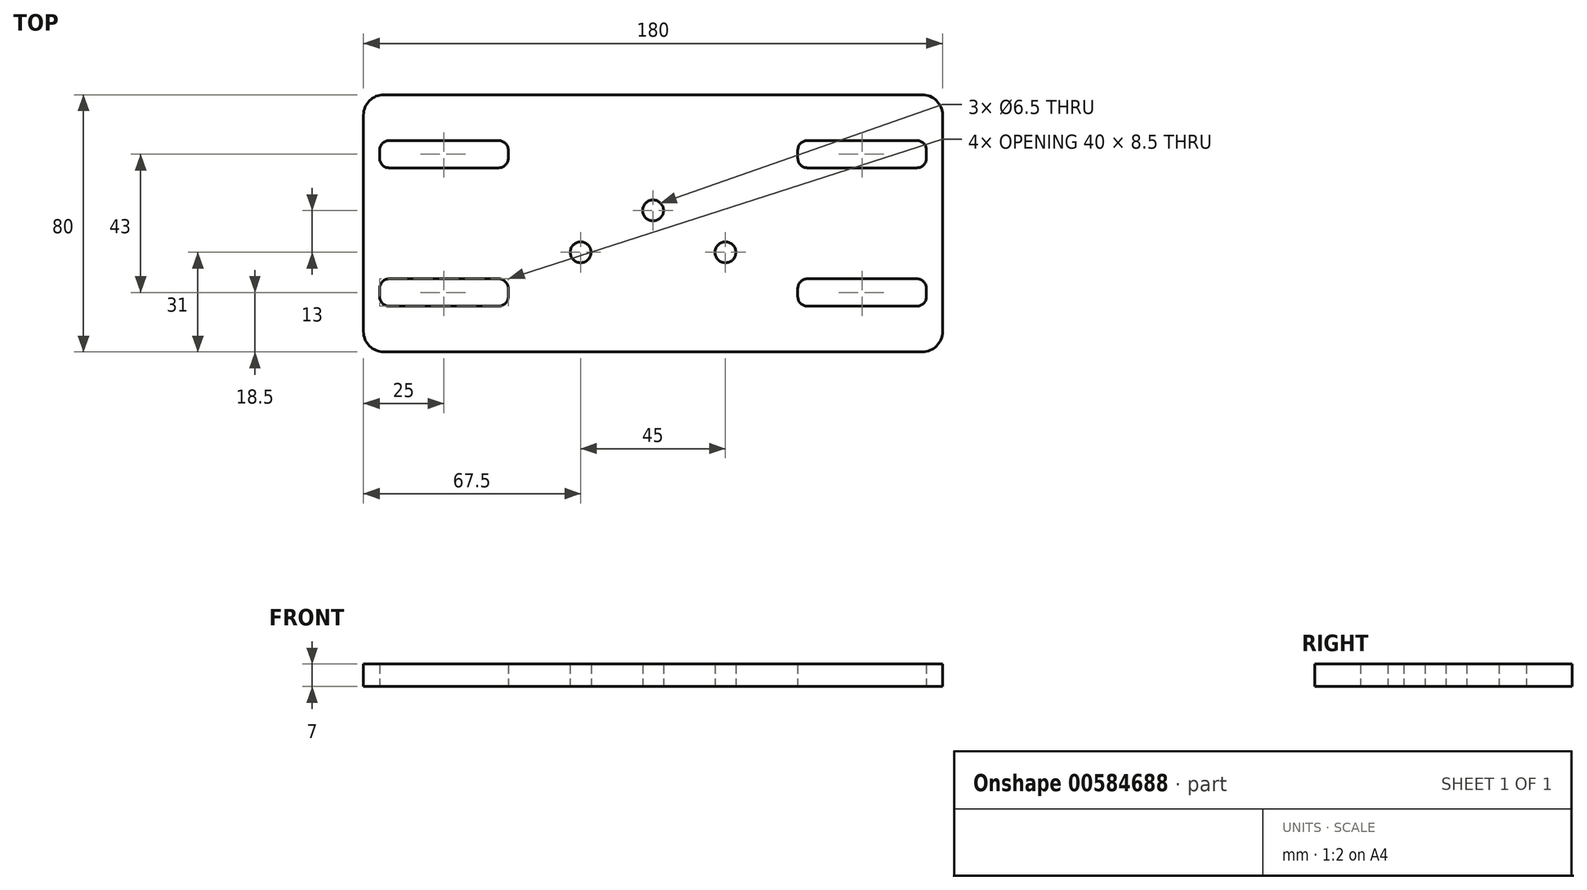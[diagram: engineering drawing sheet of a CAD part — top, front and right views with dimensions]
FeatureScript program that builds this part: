
annotation { "Feature Type Name" : "Feature", "Feature Type Description" : "" }
export const myFeature = defineFeature(function(context is Context, id is Id, definition is map)
    precondition{}
    {
        {
            var Q0;
            Q0=qCreatedBy(makeId("Top.planeOp"),FACE);
            var sketch = newSketch(context, id + "F0", { "sketchPlane" : qUnion([Q0])});
            skLineSegment(sketch, "E0.bottom", {"start": v(-83.65, 17.92) * mm, "end": v(83.65, 17.92) * mm});
            skLineSegment(sketch, "E0.top", {"start": v(-83.65, -62.08) * mm, "end": v(83.65, -62.08) * mm});
            skLineSegment(sketch, "E0.left", {"start": v(-90, 11.57) * mm, "end": v(-90, -55.73) * mm});
            skLineSegment(sketch, "E0.right", {"start": v(90, 11.57) * mm, "end": v(90, -55.73) * mm});
            skLineSegment(sketch, "E1.bottom", {"start": v(-82, -39.33) * mm, "end": v(-48, -39.33) * mm});
            skLineSegment(sketch, "E1.top", {"start": v(-82, -47.83) * mm, "end": v(-48, -47.83) * mm});
            skLineSegment(sketch, "E1.left", {"start": v(-85, -42.33) * mm, "end": v(-85, -44.83) * mm});
            skLineSegment(sketch, "E1.right", {"start": v(-45, -42.33) * mm, "end": v(-45, -44.83) * mm});
            skLineSegment(sketch, "E2", {"start": v(-120.35, -22.08) * mm, "end": v(115.73, -22.08) * mm, "construction": true});
            skPoint(sketch, "E3.visualSharp", {"position": v(-45, -39.33) * mm});
            skArc(sketch, "E3.filletArc", {"start": v(-45, -42.33) * mm, "mid": v(-45.88, -40.2) * mm, "end": v(-48, -39.33) * mm});
            skPoint(sketch, "E4.visualSharp", {"position": v(-45, -47.83) * mm});
            skArc(sketch, "E4.filletArc", {"start": v(-48, -47.83) * mm, "mid": v(-45.88, -46.95) * mm, "end": v(-45, -44.83) * mm});
            skPoint(sketch, "E5.visualSharp", {"position": v(-85, -47.83) * mm});
            skArc(sketch, "E5.filletArc", {"start": v(-85, -44.83) * mm, "mid": v(-84.12, -46.95) * mm, "end": v(-82, -47.83) * mm});
            skPoint(sketch, "E6.visualSharp", {"position": v(-85, -39.33) * mm});
            skArc(sketch, "E6.filletArc", {"start": v(-82, -39.33) * mm, "mid": v(-84.12, -40.2) * mm, "end": v(-85, -42.33) * mm});
            skCircle(sketch, "E7", {"center": v(0, -18.08) * mm, "radius": 3.25 * mm});
            skCircle(sketch, "E8", {"center": v(-22.5, -31.08) * mm, "radius": 3.25 * mm});
            skCircle(sketch, "E9.MirrorC", {"center": v(22.5, -31.08) * mm, "radius": 3.25 * mm});
            skLineSegment(sketch, "E10.MirrorCS", {"start": v(85, -42.33) * mm, "end": v(85, -44.83) * mm});
            skLineSegment(sketch, "E11.MirrorCS", {"start": v(45, -42.33) * mm, "end": v(45, -44.83) * mm});
            skArc(sketch, "E12.MirrorCS", {"start": v(85, -44.83) * mm, "mid": v(84.12, -46.95) * mm, "end": v(82, -47.83) * mm});
            skPoint(sketch, "E13.MirrorP", {"position": v(85, -47.83) * mm});
            skPoint(sketch, "E14.MirrorP", {"position": v(85, -39.33) * mm});
            skPoint(sketch, "E15.MirrorP", {"position": v(45, -39.33) * mm});
            skArc(sketch, "E16.MirrorCS", {"start": v(82, -39.33) * mm, "mid": v(84.12, -40.2) * mm, "end": v(85, -42.33) * mm});
            skArc(sketch, "E17.MirrorCS", {"start": v(48, -47.83) * mm, "mid": v(45.88, -46.95) * mm, "end": v(45, -44.83) * mm});
            skPoint(sketch, "E18.MirrorP", {"position": v(45, -47.83) * mm});
            skArc(sketch, "E19.MirrorCS", {"start": v(45, -42.33) * mm, "mid": v(45.88, -40.2) * mm, "end": v(48, -39.33) * mm});
            skLineSegment(sketch, "E20.MirrorCS", {"start": v(82, -39.33) * mm, "end": v(48, -39.33) * mm});
            skLineSegment(sketch, "E21.MirrorCS", {"start": v(82, -47.83) * mm, "end": v(48, -47.83) * mm});
            skArc(sketch, "E22.MirrorCS", {"start": v(-82, -4.83) * mm, "mid": v(-84.12, -3.95) * mm, "end": v(-85, -1.83) * mm});
            skArc(sketch, "E23.MirrorCS", {"start": v(-85, 0.67) * mm, "mid": v(-84.12, 2.8) * mm, "end": v(-82, 3.67) * mm});
            skLineSegment(sketch, "E24.MirrorCS", {"start": v(-85, -1.83) * mm, "end": v(-85, 0.67) * mm});
            skLineSegment(sketch, "E25.MirrorCS", {"start": v(85, -1.83) * mm, "end": v(85, 0.67) * mm});
            skArc(sketch, "E26.MirrorCS", {"start": v(85, 0.67) * mm, "mid": v(84.12, 2.8) * mm, "end": v(82, 3.67) * mm});
            skArc(sketch, "E27.MirrorCS", {"start": v(48, 3.67) * mm, "mid": v(45.88, 2.8) * mm, "end": v(45, 0.67) * mm});
            skArc(sketch, "E28.MirrorCS", {"start": v(-48, 3.67) * mm, "mid": v(-45.88, 2.8) * mm, "end": v(-45, 0.67) * mm});
            skArc(sketch, "E29.MirrorCS", {"start": v(-45, -1.83) * mm, "mid": v(-45.88, -3.95) * mm, "end": v(-48, -4.83) * mm});
            skLineSegment(sketch, "E30.MirrorCS", {"start": v(-45, -1.83) * mm, "end": v(-45, 0.67) * mm});
            skLineSegment(sketch, "E31.MirrorCS", {"start": v(45, -1.83) * mm, "end": v(45, 0.67) * mm});
            skArc(sketch, "E32.MirrorCS", {"start": v(82, -4.83) * mm, "mid": v(84.12, -3.95) * mm, "end": v(85, -1.83) * mm});
            skArc(sketch, "E33.MirrorCS", {"start": v(45, -1.83) * mm, "mid": v(45.88, -3.95) * mm, "end": v(48, -4.83) * mm});
            skPoint(sketch, "E34.MirrorP", {"position": v(-85, -4.83) * mm});
            skPoint(sketch, "E35.MirrorP", {"position": v(-85, 3.67) * mm});
            skPoint(sketch, "E36.MirrorP", {"position": v(85, -4.83) * mm});
            skPoint(sketch, "E37.MirrorP", {"position": v(45, 3.67) * mm});
            skLineSegment(sketch, "E38.MirrorCS", {"start": v(82, -4.83) * mm, "end": v(48, -4.83) * mm});
            skLineSegment(sketch, "E39.MirrorCS", {"start": v(82, 3.67) * mm, "end": v(48, 3.67) * mm});
            skPoint(sketch, "E40.MirrorP", {"position": v(-45, 3.67) * mm});
            skPoint(sketch, "E41.MirrorP", {"position": v(45, -4.83) * mm});
            skLineSegment(sketch, "E42.MirrorCS", {"start": v(-82, 3.67) * mm, "end": v(-48, 3.67) * mm});
            skPoint(sketch, "E43.MirrorP", {"position": v(-45, -4.83) * mm});
            skPoint(sketch, "E44.MirrorP", {"position": v(85, 3.67) * mm});
            skLineSegment(sketch, "E45.MirrorCS", {"start": v(-82, -4.83) * mm, "end": v(-48, -4.83) * mm});
            skPoint(sketch, "E46.visualSharp", {"position": v(-90, -62.08) * mm});
            skArc(sketch, "E46.filletArc", {"start": v(-90, -55.73) * mm, "mid": v(-88.14, -60.22) * mm, "end": v(-83.65, -62.08) * mm});
            skPoint(sketch, "E47.visualSharp", {"position": v(-90, 17.92) * mm});
            skArc(sketch, "E47.filletArc", {"start": v(-83.65, 17.92) * mm, "mid": v(-88.14, 16.06) * mm, "end": v(-90, 11.57) * mm});
            skPoint(sketch, "E48.visualSharp", {"position": v(90, -62.08) * mm});
            skArc(sketch, "E48.filletArc", {"start": v(83.65, -62.08) * mm, "mid": v(88.14, -60.22) * mm, "end": v(90, -55.73) * mm});
            skPoint(sketch, "E49.visualSharp", {"position": v(90, 17.92) * mm});
            skArc(sketch, "E49.filletArc", {"start": v(90, 11.57) * mm, "mid": v(88.14, 16.06) * mm, "end": v(83.65, 17.92) * mm});
            skSolve(sketch);
        }
        {
            var Q0;
            Q0=makeQuery(id+"F0.imprint","IMPRINT",FACE,{"disambiguationData":[TD([[makeQuery(id+"F0.imprint","IMPRINT",EDGE,{"derivedFrom":sQuery(id+"F0.wireOp",EDGE,"E0.bottom")}),-1.0]])]});
            extrude(context, id + "F1", {"entities" : qUnion([Q0]), "depth" : 7 * mm, "offsetDistance" : 25 * mm});
        }
    });
